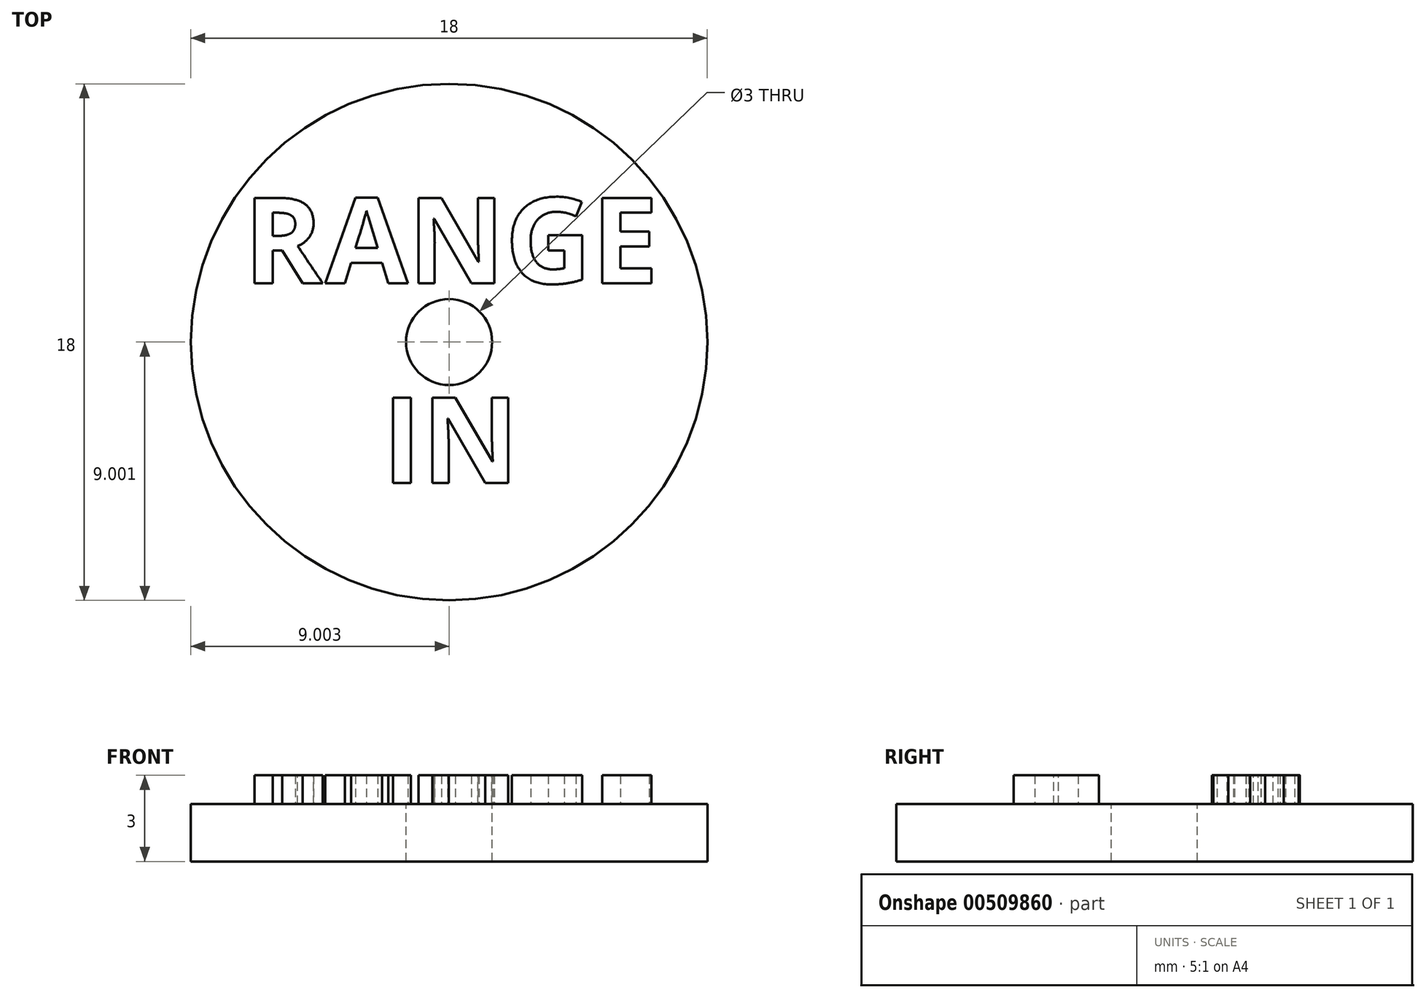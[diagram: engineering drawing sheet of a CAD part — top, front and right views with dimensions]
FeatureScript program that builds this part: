
annotation { "Feature Type Name" : "Feature", "Feature Type Description" : "" }
export const myFeature = defineFeature(function(context is Context, id is Id, definition is map)
    precondition{}
    {
        {
            var Q0;
            Q0=qCreatedBy(makeId("Top.planeOp"),FACE);
            var sketch = newSketch(context, id + "F0", { "sketchPlane" : qUnion([Q0])});
            skCircle(sketch, "E0", {"center": v(-42.4, -34.64) * mm, "radius": 9 * mm});
            skSolve(sketch);
        }
        {
            var Q0;
            Q0=qSketchRegion(id+"F0",true);
            extrude(context, id + "F1", {"entities" : qUnion([Q0]), "depth" : 2 * mm, "offsetDistance" : 25 * mm});
        }
        {
            var Q0;
            Q0=makeQuery(id+"F1.opExtrude","CAP_FACE",FACE,{"disambiguationData":[OSD([sQuery(id+"F0.wireOp",EDGE,"E0")])],"isStart":false});
            var sketch = newSketch(context, id + "F2", { "sketchPlane" : qUnion([Q0])});
            skCircle(sketch, "E1", {"center": v(-42.4, -34.64) * mm, "radius": 1.5 * mm});
            skSolve(sketch);
        }
        {
            var Q0;
            Q0 = qSketchRegion(id + "F2", true);
            extrude(context, id + "F3", {"entities" : qUnion([Q0]), "operationType" : NewBodyOperationType.REMOVE, "oppositeDirection" : true, "depth" : 2 * mm, "offsetDistance" : 25 * mm});
        }
        {
            var Q0;
            Q0=makeQuery(id+"F1.opExtrude","CAP_FACE",FACE,{"disambiguationData":[OSD([sQuery(id+"F0.wireOp",EDGE,"E0")])],"isStart":false});
            var sketch = newSketch(context, id + "F4", { "sketchPlane" : qUnion([Q0])});
            skText(sketch, "E2", { "text": "RANGE", "fontName": "OpenSans-Bold.ttf"});
            skText(sketch, "E3", { "text": "IN", "fontName": "OpenSans-Bold.ttf"});
            const initialGuessF4  = {"E2": [-0.04956, -0.03259, 1, 0, 0.003], "E3": [-0.04474, -0.03955, 1, 0, 0.003]};
            skSetInitialGuess(sketch, initialGuessF4);
            skSolve(sketch);
        }
        {
            var Q0;
            Q0 = qSketchRegion(id + "F4", true);
            extrude(context, id + "F5", {"entities" : qUnion([Q0]), "depth" : 1 * mm, "offsetDistance" : 25 * mm});
        }
    });
